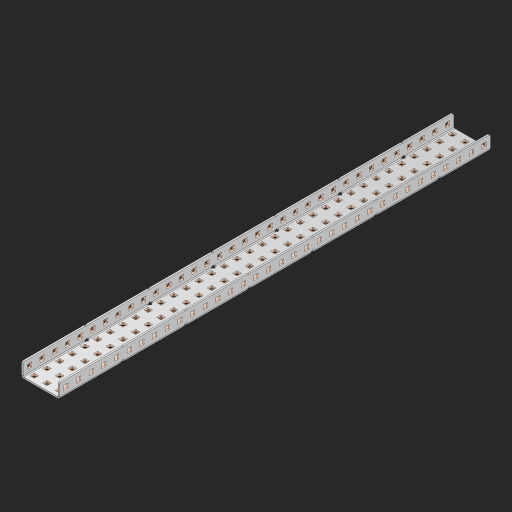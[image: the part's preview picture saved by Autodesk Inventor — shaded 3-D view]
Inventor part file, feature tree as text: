
AUTODESK INVENTOR PART (.ipt)
format: ipt  version: 2023 (Build 270158000, 158)  size: 1,994,240 bytes
history: native  units: in
note: dims shown in document units (in); Inventor stores cm internally (conversion verified against a paired STEP export)
features: other x175, extrude x169, sheet_metal_op x10, sketch x8, mirror x1, pattern_linear x1, chamfer x1
ambient origin geometry x8: Origin, YZ Plane, XZ Plane, XY Plane, X Axis, Y Axis, Z Axis, Center Point
bodies: Solid1 (feature_tree), Body (feature_tree)
feature tree (365):
  other  "Flange Pattern Plane"
  sheet_metal_op  "Flange Pattern"
  sheet_metal_op  "Body Pattern"
  other  "Arc Length"
  mirror  "Notch Mirror"
  pattern_linear  "Notch Pattern"  Spacing1=0.25in  [1 undecoded]
  chamfer  "End Chamfer"
  extrude  "Half Cut"  Depth=0.0625in
  sketch  "Sketch1"  dims[d0=1.5in]
  other  "Plate1"
  sketch  "Sketch2"  dims[d1=17.0in]
  other  "Plate2"
  sheet_metal_op  "Bend1"
  sheet_metal_op  "Corner1"
  sketch  "Sketch3"  dims[d2=0.0625in]
  other  "Flange Pattern Sketch"
  sketch  "Sketch7"  dims[d3=0.0625in]
  other  "Srf1"
  other  "Srf2"
  sketch  "Sketch8"  dims[d4=0.0312in]
  sketch  "Sketch9"  dims[d5=0.125in]
  other  "Srf91"
  sheet_metal_op  "Body Pattern Sketch"
  other  "Srf92"
  sketch  "Sketch13"  dims[d6=0.0625in]
  sketch  "Sketch14"  dims[d7=0.5in d8=90.0deg d9=0.0312in d10=0.25in d11=0.0625in d12=0.0625in d16=0.182in d17=0.02in d18=0.0625in d19=0.0in d20=0.25in d21=0.25in d46=0.172in d47=1.0in d48=0.0in d49=0.182in d50=0.02in d51=0.25in d52=0.25in d53=0.0625in d54=0.0in d55=0.172in d56=1.0in d57=0.0in d60=13.3858in d62=0.5in d63=1.1811in d65=0.5in d85=0.1473in d86=0.1782in d88=0.04in d89=0.0625in d90=0.0in d91=0.04in d92=0.0491in d95=2.5in d96=0.04in d97=0.25in d98=45.0deg d101=0.0in d102=2.497in d131=1.5in d132=13.3858in d134=0.5in d139=0.5in]
  other  "Srf856"
  other  "Srf1310"
  other  "Srf1311"
  other  "Srf1312"
  other  "Srf1376"
  other  "Srf1377"
  other  "Srf1728"
  other  "Srf1755"
  other  "Srf1878"
  other  "Srf1879"
  other  "Srf1880"
  other  "Srf1881"
  other  "Srf1882"
  other  "Srf1883"
  other  "Srf1884"
  other  "Srf1885"
  other  "Srf1886"
  other  "Srf1887"
  other  "Srf1888"
  other  "Srf1889"
  other  "Srf1890"
  other  "Srf1891"
  other  "Srf1892"
  other  "Srf1893"
  other  "Srf1894"
  other  "Srf1895"
  other  "Srf1896"
  other  "Srf1897"
  other  "Srf1898"
  other  "Srf1899"
  other  "Srf1900"
  other  "Srf1901"
  other  "Srf1902"
  other  "Srf1903"
  other  "Srf1904"
  other  "Srf1905"
  other  "Srf1906"
  other  "Srf1907"
  other  "Srf1908"
  other  "Srf1909"
  other  "Srf1910"
  other  "Srf1911"
  other  "Srf1912"
  other  "Srf1913"
  other  "Srf1914"
  other  "Srf1915"
  other  "Srf1916"
  other  "Srf1917"
  other  "Srf1918"
  other  "Srf1919"
  other  "Srf1920"
  other  "Srf1921"
  other  "Srf1922"
  other  "Srf1923"
  other  "Srf1924"
  other  "Srf1925"
  other  "Srf1926"
  other  "Srf1927"
  other  "Srf1928"
  other  "Srf1929"
  other  "Srf1930"
  other  "Srf1931"
  other  "Srf1932"
  other  "Srf1933"
  other  "Srf1934"
  other  "Srf1935"
  other  "Srf1936"
  other  "Srf1937"
  other  "Srf1938"
  other  "Srf1939"
  other  "Srf1942"
  other  "Srf1943"
  other  "Srf1944"
  other  "Srf1945"
  other  "Srf1946"
  other  "Srf1947"
  other  "Srf1948"
  other  "Srf1949"
  other  "Srf1950"
  other  "Srf1951"
  other  "Srf1952"
  other  "Srf1953"
  other  "Srf1954"
  other  "Srf1955"
  other  "Srf1956"
  other  "Srf1957"
  other  "Srf1958"
  other  "Srf1959"
  other  "Srf1960"
  other  "Srf1961"
  other  "Srf1962"
  other  "Srf1963"
  other  "Srf1964"
  other  "Srf1965"
  other  "Srf1966"
  other  "Srf1967"
  other  "Srf1968"
  other  "Srf1969"
  other  "Srf1970"
  other  "Srf1971"
  other  "Srf1972"
  other  "Srf1973"
  other  "Srf1974"
  other  "Srf1975"
  other  "Srf1976"
  other  "Srf1977"
  other  "Srf1978"
  other  "Srf1979"
  other  "Srf1980"
  other  "Srf1981"
  other  "Srf1982"
  other  "Srf1983"
  other  "Srf1984"
  other  "Srf1985"
  other  "Srf1986"
  other  "Srf1987"
  other  "Srf1988"
  other  "Srf1989"
  other  "Srf1990"
  other  "Srf1991"
  other  "Srf1992"
  other  "Srf1993"
  other  "Srf1994"
  other  "Srf1995"
  other  "Srf1996"
  other  "Srf1997"
  other  "Srf1998"
  other  "Srf1999"
  other  "Srf2000"
  other  "Srf2001"
  other  "Srf2002"
  other  "Srf2003"
  other  "Srf2004"
  other  "Srf2005"
  other  "Srf2006"
  other  "Srf2007"
  other  "Srf2008"
  other  "Srf2009"
  other  "Srf2010"
  other  "Srf2011"
  other  "Srf2012"
  other  "Srf2013"
  other  "Srf2014"
  other  "Srf2015"
  other  "Srf2016"
  other  "Srf2017"
  other  "Srf2018"
  other  "Srf2019"
  other  "Srf2020"
  other  "Srf2021"
  other  "Srf2022"
  other  "Srf2023"
  other  "Srf2024"
  other  "Srf2025"
  other  "Srf2026"
  other  "Srf2027"
  other  "Srf2028"
  other  "Srf2029"
  other  "Srf2030"
  other  "Srf2031"
  other  "Srf2032"
  other  "Srf2033"
  other  "Srf2034"
  other  "Srf2035"
  other  "Srf2036"
  other  "Srf2037"
  sheet_metal_op  "Flange Stamp"
  sheet_metal_op  "Flange Circle"
  sheet_metal_op  "Body Stamp"
  sheet_metal_op  "Body Circle"
  sheet_metal_op  "Notch"
  extrude  "ExtrusionSrf2"  Depth=0.0625in
  extrude  "ExtrusionSrf92"  Depth=1.5in
  extrude  "ExtrusionSrf856"  Depth=0.02in
  extrude  "ExtrusionSrf1310"  Depth=0.0625in
  extrude  "ExtrusionSrf1311"  TaperAngle=0.0deg  [1 undecoded]
  extrude  "ExtrusionSrf1312"  Depth=0.25in
  extrude  "ExtrusionSrf1376"  Depth=0.25in
  extrude  "ExtrusionSrf1377"  Depth=1.5in
  extrude  "ExtrusionSrf1728"  Depth=1.5in TaperAngle=0.0deg
  extrude  "ExtrusionSrf1755"  Depth=1.5in
  extrude  "ExtrusionSrf1878"  Depth=0.02in
  extrude  "ExtrusionSrf1879"  Depth=0.25in
  extrude  "ExtrusionSrf1880"  Depth=0.25in
  extrude  "ExtrusionSrf1881"  Depth=0.0625in
  extrude  "ExtrusionSrf1882"  TaperAngle=0.0deg  [1 undecoded]
  extrude  "ExtrusionSrf1883"  Depth=1.5in
  extrude  "ExtrusionSrf1884"  Depth=1.5in TaperAngle=0.0deg
  extrude  "ExtrusionSrf1885"  Depth=1.5in
  extrude  "ExtrusionSrf1886"  Depth=1.5in
  extrude  "ExtrusionSrf1887"  Depth=1.5in
  extrude  "ExtrusionSrf1888"  Depth=1.5in
  extrude  "ExtrusionSrf1889"  Depth=1.5in
  extrude  "ExtrusionSrf1890"  Depth=0.0625in
  extrude  "ExtrusionSrf1891"  TaperAngle=0.0deg  [1 undecoded]
  extrude  "ExtrusionSrf1892"  Depth=1.5in
  extrude  "ExtrusionSrf1893"  Depth=1.5in
  extrude  "ExtrusionSrf1894"  Depth=1.5in
  extrude  "ExtrusionSrf1895"  Depth=0.25in TaperAngle=45.0deg
  extrude  "ExtrusionSrf1896"  TaperAngle=0.0deg  [1 undecoded]
  extrude  "ExtrusionSrf1897"  Depth=1.5in
  extrude  "ExtrusionSrf1898"  Depth=1.5in
  extrude  "ExtrusionSrf1899"  Depth=1.5in
  extrude  "ExtrusionSrf1900"  Depth=1.5in
  extrude  "ExtrusionSrf1901"  Depth=1.5in
  extrude  "ExtrusionSrf1902"  [1 undecoded]
  extrude  "ExtrusionSrf1903"  [1 undecoded]
  extrude  "ExtrusionSrf1904"  [1 undecoded]
  extrude  "ExtrusionSrf1905"  [1 undecoded]
  extrude  "ExtrusionSrf1906"  [1 undecoded]
  extrude  "ExtrusionSrf1907"  [1 undecoded]
  extrude  "ExtrusionSrf1908"  [1 undecoded]
  extrude  "ExtrusionSrf1909"  [1 undecoded]
  extrude  "ExtrusionSrf1910"  [1 undecoded]
  extrude  "ExtrusionSrf1911"  [1 undecoded]
  extrude  "ExtrusionSrf1912"  [1 undecoded]
  extrude  "ExtrusionSrf1913"  [1 undecoded]
  extrude  "ExtrusionSrf1914"  [1 undecoded]
  extrude  "ExtrusionSrf1915"  [1 undecoded]
  extrude  "ExtrusionSrf1916"  [1 undecoded]
  extrude  "ExtrusionSrf1917"  [1 undecoded]
  extrude  "ExtrusionSrf1918"  [1 undecoded]
  extrude  "ExtrusionSrf1919"  [1 undecoded]
  extrude  "ExtrusionSrf1920"  [1 undecoded]
  extrude  "ExtrusionSrf1921"  [1 undecoded]
  extrude  "ExtrusionSrf1922"  [1 undecoded]
  extrude  "ExtrusionSrf1923"  [1 undecoded]
  extrude  "ExtrusionSrf1924"  [1 undecoded]
  extrude  "ExtrusionSrf1925"  [1 undecoded]
  extrude  "ExtrusionSrf1926"  [1 undecoded]
  extrude  "ExtrusionSrf1927"  [1 undecoded]
  extrude  "ExtrusionSrf1928"  [1 undecoded]
  extrude  "ExtrusionSrf1929"  [1 undecoded]
  extrude  "ExtrusionSrf1930"  [1 undecoded]
  extrude  "ExtrusionSrf1931"  [1 undecoded]
  extrude  "ExtrusionSrf1932"  [1 undecoded]
  extrude  "ExtrusionSrf1933"  [1 undecoded]
  extrude  "ExtrusionSrf1934"  [1 undecoded]
  extrude  "ExtrusionSrf1935"  [1 undecoded]
  extrude  "ExtrusionSrf1936"  [1 undecoded]
  extrude  "ExtrusionSrf1937"  [1 undecoded]
  extrude  "ExtrusionSrf1938"  [1 undecoded]
  extrude  "ExtrusionSrf1939"  [1 undecoded]
  extrude  "ExtrusionSrf1942"  [1 undecoded]
  extrude  "ExtrusionSrf1943"  [1 undecoded]
  extrude  "ExtrusionSrf1944"  [1 undecoded]
  extrude  "ExtrusionSrf1945"  [1 undecoded]
  extrude  "ExtrusionSrf1946"  [1 undecoded]
  extrude  "ExtrusionSrf1947"  [1 undecoded]
  extrude  "ExtrusionSrf1948"  [1 undecoded]
  extrude  "ExtrusionSrf1949"  [1 undecoded]
  extrude  "ExtrusionSrf1950"  [1 undecoded]
  extrude  "ExtrusionSrf1951"  [1 undecoded]
  extrude  "ExtrusionSrf1952"  [1 undecoded]
  extrude  "ExtrusionSrf1953"  [1 undecoded]
  extrude  "ExtrusionSrf1954"  [1 undecoded]
  extrude  "ExtrusionSrf1955"  [1 undecoded]
  extrude  "ExtrusionSrf1956"  [1 undecoded]
  extrude  "ExtrusionSrf1957"  [1 undecoded]
  extrude  "ExtrusionSrf1958"  [1 undecoded]
  extrude  "ExtrusionSrf1959"  [1 undecoded]
  extrude  "ExtrusionSrf1960"  [1 undecoded]
  extrude  "ExtrusionSrf1961"  [1 undecoded]
  extrude  "ExtrusionSrf1962"  [1 undecoded]
  extrude  "ExtrusionSrf1963"  [1 undecoded]
  extrude  "ExtrusionSrf1964"  [1 undecoded]
  extrude  "ExtrusionSrf1965"  [1 undecoded]
  extrude  "ExtrusionSrf1966"  [1 undecoded]
  extrude  "ExtrusionSrf1967"  [1 undecoded]
  extrude  "ExtrusionSrf1968"  [1 undecoded]
  extrude  "ExtrusionSrf1969"  [1 undecoded]
  extrude  "ExtrusionSrf1970"  [1 undecoded]
  extrude  "ExtrusionSrf1971"  [1 undecoded]
  extrude  "ExtrusionSrf1972"  [1 undecoded]
  extrude  "ExtrusionSrf1973"  [1 undecoded]
  extrude  "ExtrusionSrf1974"  [1 undecoded]
  extrude  "ExtrusionSrf1975"  [1 undecoded]
  extrude  "ExtrusionSrf1976"  [1 undecoded]
  extrude  "ExtrusionSrf1977"  [1 undecoded]
  extrude  "ExtrusionSrf1978"  [1 undecoded]
  extrude  "ExtrusionSrf1979"  [1 undecoded]
  extrude  "ExtrusionSrf1980"  [1 undecoded]
  extrude  "ExtrusionSrf1981"  [1 undecoded]
  extrude  "ExtrusionSrf1982"  [1 undecoded]
  extrude  "ExtrusionSrf1983"  [1 undecoded]
  extrude  "ExtrusionSrf1984"  [1 undecoded]
  extrude  "ExtrusionSrf1985"  [1 undecoded]
  extrude  "ExtrusionSrf1986"  [1 undecoded]
  extrude  "ExtrusionSrf1987"  [1 undecoded]
  extrude  "ExtrusionSrf1988"  [1 undecoded]
  extrude  "ExtrusionSrf1989"  [1 undecoded]
  extrude  "ExtrusionSrf1990"  [1 undecoded]
  extrude  "ExtrusionSrf1991"  [1 undecoded]
  extrude  "ExtrusionSrf1992"  [1 undecoded]
  extrude  "ExtrusionSrf1993"  [1 undecoded]
  extrude  "ExtrusionSrf1994"  [1 undecoded]
  extrude  "ExtrusionSrf1995"  [1 undecoded]
  extrude  "ExtrusionSrf1996"  [1 undecoded]
  extrude  "ExtrusionSrf1997"  [1 undecoded]
  extrude  "ExtrusionSrf1998"  [1 undecoded]
  extrude  "ExtrusionSrf1999"  [1 undecoded]
  extrude  "ExtrusionSrf2000"  [1 undecoded]
  extrude  "ExtrusionSrf2001"  [1 undecoded]
  extrude  "ExtrusionSrf2002"  [1 undecoded]
  extrude  "ExtrusionSrf2003"  [1 undecoded]
  extrude  "ExtrusionSrf2004"  [1 undecoded]
  extrude  "ExtrusionSrf2005"  [1 undecoded]
  extrude  "ExtrusionSrf2006"  [1 undecoded]
  extrude  "ExtrusionSrf2007"  [1 undecoded]
  extrude  "ExtrusionSrf2008"  [1 undecoded]
  extrude  "ExtrusionSrf2009"  [1 undecoded]
  extrude  "ExtrusionSrf2010"  [1 undecoded]
  extrude  "ExtrusionSrf2011"  [1 undecoded]
  extrude  "ExtrusionSrf2012"  [1 undecoded]
  extrude  "ExtrusionSrf2013"  [1 undecoded]
  extrude  "ExtrusionSrf2014"  [1 undecoded]
  extrude  "ExtrusionSrf2015"  [1 undecoded]
  extrude  "ExtrusionSrf2016"  [1 undecoded]
  extrude  "ExtrusionSrf2017"  [1 undecoded]
  extrude  "ExtrusionSrf2018"  [1 undecoded]
  extrude  "ExtrusionSrf2019"  [1 undecoded]
  extrude  "ExtrusionSrf2020"  [1 undecoded]
  extrude  "ExtrusionSrf2021"  [1 undecoded]
  extrude  "ExtrusionSrf2022"  [1 undecoded]
  extrude  "ExtrusionSrf2023"  [1 undecoded]
  extrude  "ExtrusionSrf2024"  [1 undecoded]
  extrude  "ExtrusionSrf2025"  [1 undecoded]
  extrude  "ExtrusionSrf2026"  [1 undecoded]
  extrude  "ExtrusionSrf2027"  [1 undecoded]
  extrude  "ExtrusionSrf2028"  [1 undecoded]
  extrude  "ExtrusionSrf2029"  [1 undecoded]
  extrude  "ExtrusionSrf2030"  [1 undecoded]
  extrude  "ExtrusionSrf2031"  [1 undecoded]
  extrude  "ExtrusionSrf2032"  [1 undecoded]
  extrude  "ExtrusionSrf2033"  [1 undecoded]
  extrude  "ExtrusionSrf2034"  [1 undecoded]
  extrude  "ExtrusionSrf2035"  [1 undecoded]
  extrude  "ExtrusionSrf2036"  [1 undecoded]
  extrude  "ExtrusionSrf2037"  [1 undecoded]
note: 139 required parameter values undecoded (feature->parameter linkage not recoverable at this tier; creation-order binding heuristic only, values carry confidence <= 0.55)
